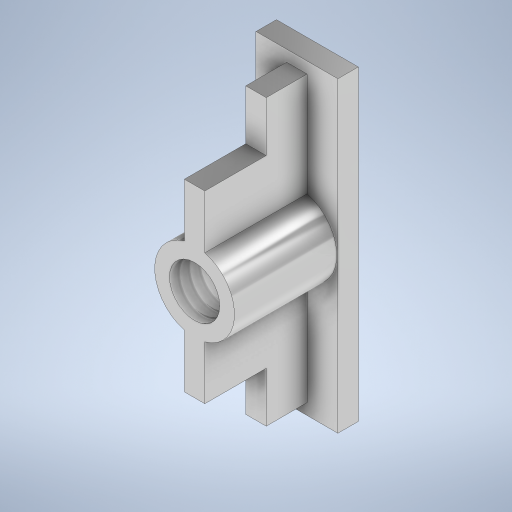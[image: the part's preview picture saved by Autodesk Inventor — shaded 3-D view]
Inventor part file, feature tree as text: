
AUTODESK INVENTOR PART (.ipt)
format: ipt  version: 2023 (Build 270158000, 158)  size: 307,712 bytes
history: native  units: mm
features: sketch x5, extrude x4, other x1, hole x1
ambient origin geometry x8: Origin, YZ Plane, XZ Plane, XY Plane, X Axis, Y Axis, Z Axis, Center Point
bodies: Body1 (feature_tree)
feature tree (11):
  other  "Sólido1"
  extrude  "Extrusão1"  Depth=15.0mm
  extrude  "Extrusão2"  Depth=1.0mm
  extrude  "Extrusão3"  Depth=5.0mm TaperAngle=0.0deg
  extrude  "Extrusão4"  Depth=1.0mm
  hole  "Furo1"  [1 undecoded]
  sketch  "Esboço1"  dims[d0=4.0mm d1=15.0mm]
  sketch  "Esboço2"  dims[d2=1.0mm d3=0.0mm d4=3.9mm]
  sketch  "Esboço3"  dims[d5=13.9mm d6=5.0mm d7=0.0mm]
  sketch  "Esboço4"  dims[d8=3.9mm d9=1.0mm]
  sketch  "Esboço5"  dims[d10=5.0mm d11=0.0mm d12=1.0mm d13=9.0mm d14=3.0mm d15=0.0mm d16=2.459mm d17=6.0mm d18=4.0mm d19=2.0mm d20=90.0deg d21=8.0mm d22=20.594885mm d23=0.0mm d24=0.0mm]
note: 1 required parameter value undecoded (feature->parameter linkage not recoverable at this tier; creation-order binding heuristic only, values carry confidence <= 0.55)
